# Revit family: Fireplace_Gas_HeatNGlo_Lanai
name_source: partatom
category: Mechanical Equipment
revit_build: Autodesk Revit 2015 (Build: 20140606_1530(x64)
units: mm (PartAtom-declared; Revit-internal decimal feet)

## types (2) — shared parameters
Assembly Code = D3020
Construction Details = https://www.arcat.com
Default Elevation = 0' - 0"
Description = Heat & Glo Outdoor Gas Burning Fireplace - Lanai as Specified
Efficiency Ratings = as Specified
Electrical_Amperage = 0 A
Electrical_Frequency = 0 Hz
Electrical_Voltage = 0 V
Fixture Finish = Metal - HHT - Stainless Steel
Fuel Consumption = as Specified
Green Building-LEED = https://www.arcat.com
HVAC_BTU Output = 0.0 Btu/h
Heating Capacity = as Specified
Keynote = 10 31 00
Manufacturer = Heat & Glo
Manufacturer Website = http://pro.heatnglo.com
Model = ODLANAIG-51
Opening Height = 1' - 6"
Opening Width = 4' - 3"
Product Data = https://www.arcat.com
Revision = R1_2018-05
Sales Information = http://pro.heatnglo.com
SpecWizard = https://www.arcat.com
Specification = https://www.arcat.com
Standards Conformance = cULus  ;  ANSI Z21.97-2014  ;  CSA 2.41-2014
URL = http://pro.heatnglo.com
Unit Depth = 1' - 5 5/8"
Unit Height = 2' - 6 3/8"
Unit Width = 4' - 9 1/4"
zero-valued in all types: Expected Lifespan (Years), Maintenance Schedule (Months), Unit Weight, Warranty Duration (Years)

## per-type parameters (varying)
| type | Fuel Type | HVAC_BTU Input |
| 51 x 18 Viewing Area NG | Natural Gas | 55000.0 Btu/h |
| 51 x 18 Viewing Area LP | Liquid Petroleum | 53000.0 Btu/h |

## geometry (parser evidence)
native form markers: Sweep x3
no freeform markers — native parametric forms only
